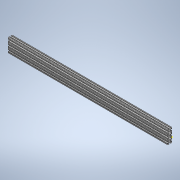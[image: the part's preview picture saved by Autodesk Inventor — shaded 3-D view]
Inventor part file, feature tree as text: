
AUTODESK INVENTOR PART (.ipt)
format: ipt  version: 2020 (Build 240168000, 168)  size: 397,312 bytes
history: native  units: in
note: dims shown in document units (in); Inventor stores cm internally (conversion verified against a paired STEP export)
features: sketch x2, extrude x1
ambient origin geometry x8: Origin, YZ Plane, XZ Plane, XY Plane, X Axis, Y Axis, Z Axis, Center Point
bodies: Solid1 (feature_tree)
feature tree (3):
  extrude  "Extrusion1"  [1 undecoded]
  sketch  "Sketch2"
  sketch  "Sketch1"  dims[d0=35.0in d1=0.0in]
note: 1 required parameter value undecoded (feature->parameter linkage not recoverable at this tier; creation-order binding heuristic only, values carry confidence <= 0.55)
